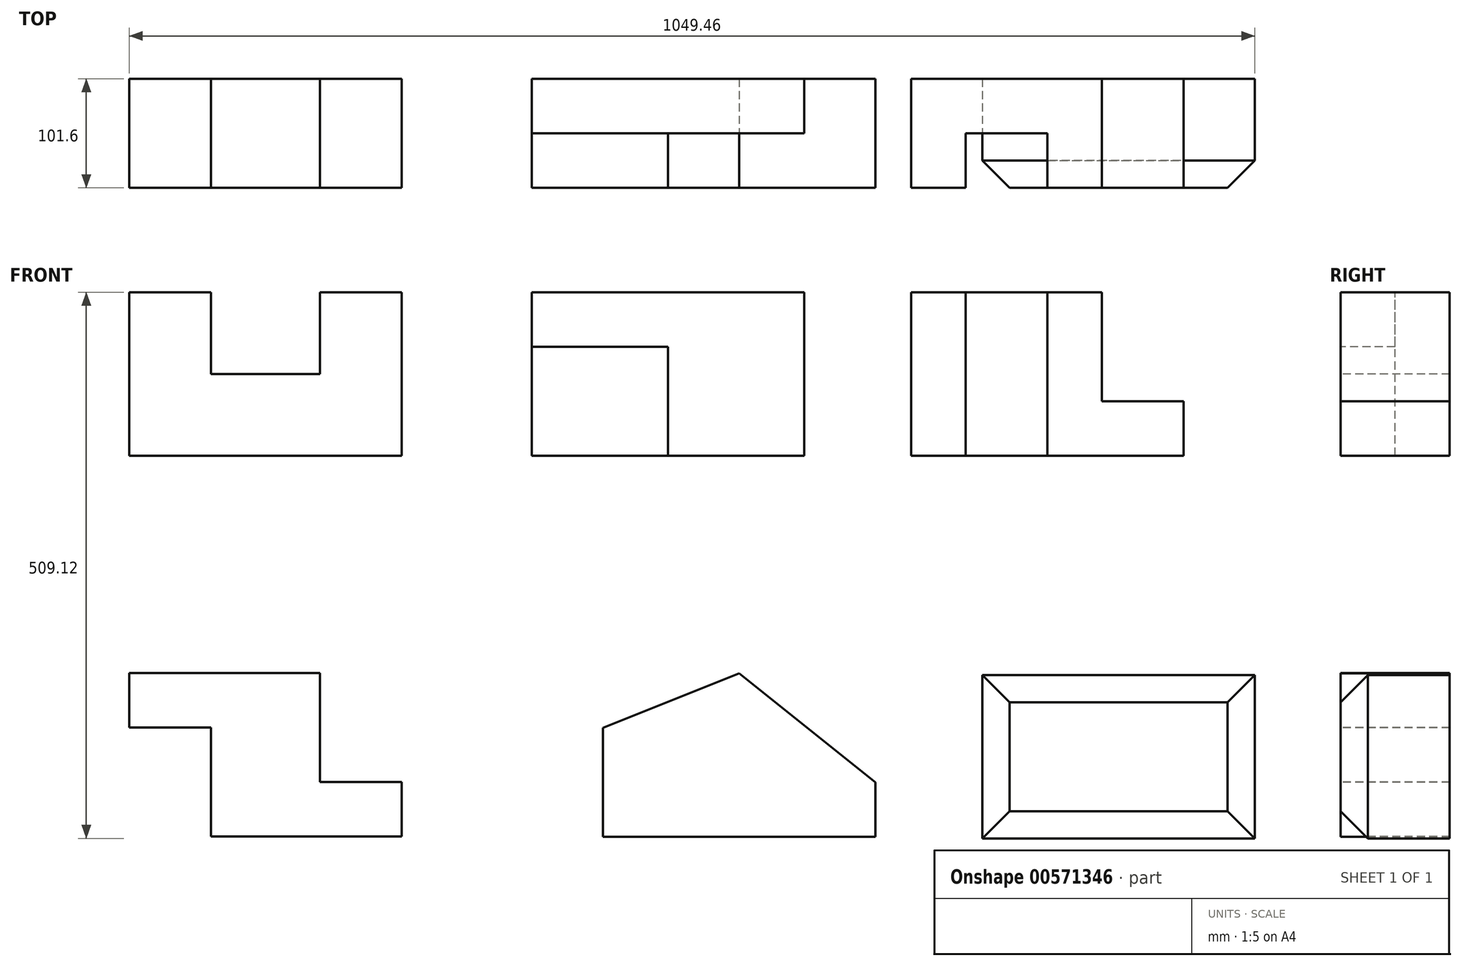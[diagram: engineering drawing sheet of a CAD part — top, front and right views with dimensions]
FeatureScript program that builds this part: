
annotation { "Feature Type Name" : "Feature", "Feature Type Description" : "" }
export const myFeature = defineFeature(function(context is Context, id is Id, definition is map)
    precondition{}
    {
        {
            var Q0;
            Q0=qCreatedBy(makeId("Front.planeOp"),FACE);
            var sketch = newSketch(context, id + "F0", { "sketchPlane" : qUnion([Q0])});
            skLineSegment(sketch, "E0", {"start": v(0, 0) * mm, "end": v(254, 0) * mm});
            skLineSegment(sketch, "E1", {"start": v(254, 0) * mm, "end": v(254, 152.4) * mm});
            skLineSegment(sketch, "E2", {"start": v(254, 152.4) * mm, "end": v(177.8, 152.4) * mm});
            skLineSegment(sketch, "E3", {"start": v(177.8, 152.4) * mm, "end": v(177.8, 76.2) * mm});
            skLineSegment(sketch, "E4", {"start": v(177.8, 76.2) * mm, "end": v(76.2, 76.2) * mm});
            skLineSegment(sketch, "E5", {"start": v(76.2, 76.2) * mm, "end": v(76.2, 152.4) * mm});
            skLineSegment(sketch, "E6", {"start": v(76.2, 152.4) * mm, "end": v(0, 152.4) * mm});
            skLineSegment(sketch, "E7", {"start": v(0, 152.4) * mm, "end": v(0, 0) * mm});
            skSolve(sketch);
        }
        {
            var Q0;
            Q0=makeQuery(id+"F0.imprint","IMPRINT",FACE,{"disambiguationData":[TD([[makeQuery(id+"F0.imprint","IMPRINT",EDGE,{"derivedFrom":sQuery(id+"F0.wireOp",EDGE,"E0")}),1.0]])]});
            extrude(context, id + "F1", {"entities" : qUnion([Q0]), "oppositeDirection" : true, "depth" : 101.6 * mm, "offsetDistance" : 25.4 * mm});
        }
        {
            var Q0;
            Q0=qCreatedBy(makeId("Front.planeOp"),FACE);
            var sketch = newSketch(context, id + "F2", { "sketchPlane" : qUnion([Q0])});
            skLineSegment(sketch, "E8.bottom", {"start": v(375.22, 0) * mm, "end": v(629.22, 0) * mm});
            skLineSegment(sketch, "E8.top", {"start": v(375.22, 152.4) * mm, "end": v(629.22, 152.4) * mm});
            skLineSegment(sketch, "E8.left", {"start": v(375.22, 0) * mm, "end": v(375.22, 152.4) * mm});
            skLineSegment(sketch, "E8.right", {"start": v(629.22, 0) * mm, "end": v(629.22, 152.4) * mm});
            skSolve(sketch);
        }
        {
            var Q0;
            Q0=makeQuery(id+"F2.imprint","IMPRINT",FACE,{"disambiguationData":[TD([[makeQuery(id+"F2.imprint","IMPRINT",EDGE,{"derivedFrom":sQuery(id+"F2.wireOp",EDGE,"E8.bottom")}),1.0]])]});
            extrude(context, id + "F3", {"entities" : qUnion([Q0]), "oppositeDirection" : true, "depth" : 101.6 * mm, "offsetDistance" : 25.4 * mm});
        }
        {
            var Q0;
            Q0=makeQuery(id+"F3.opExtrude","SWEPT_FACE",FACE,{"disambiguationData":[OSD([sQuery(id+"F2.wireOp",EDGE,"E8.top")])]});
            var sketch = newSketch(context, id + "F4", { "sketchPlane" : qUnion([Q0])});
            skLineSegment(sketch, "E9.bottom", {"start": v(629.22, 0) * mm, "end": v(502.22, 0) * mm});
            skLineSegment(sketch, "E9.top", {"start": v(629.22, 50.8) * mm, "end": v(502.22, 50.8) * mm});
            skLineSegment(sketch, "E9.left", {"start": v(629.22, 0) * mm, "end": v(629.22, 50.8) * mm});
            skLineSegment(sketch, "E9.right", {"start": v(502.22, 0) * mm, "end": v(502.22, 50.8) * mm});
            skSolve(sketch);
        }
        {
            var Q0;
            Q0=makeQuery(id+"F4.imprint","IMPRINT",FACE,{"disambiguationData":[TD([[makeQuery(id+"F4.imprint","IMPRINT",EDGE,{"derivedFrom":sQuery(id+"F4.wireOp",EDGE,"E9.bottom")}),1.0]])]});
            extrude(context, id + "F5", {"entities" : qUnion([Q0]), "operationType" : NewBodyOperationType.REMOVE, "oppositeDirection" : true, "depth" : 152.4 * mm, "offsetDistance" : 25.4 * mm});
        }
        {
            var Q0;
            Q0=makeQuery(id+"F3.opExtrude","CAP_FACE",FACE,{"disambiguationData":[OSD([sQuery(id+"F2.wireOp",EDGE,"E8.bottom"),sQuery(id+"F2.wireOp",EDGE,"E8.top"),sQuery(id+"F2.wireOp",EDGE,"E8.left"),sQuery(id+"F2.wireOp",EDGE,"E8.right")])],"isStart":true});
            var sketch = newSketch(context, id + "F6", { "sketchPlane" : qUnion([Q0])});
            skLineSegment(sketch, "E10", {"start": v(502.22, 152.4) * mm, "end": v(375.22, 152.4) * mm});
            skLineSegment(sketch, "E11", {"start": v(375.22, 152.4) * mm, "end": v(375.22, 101.6) * mm});
            skLineSegment(sketch, "E12", {"start": v(375.22, 101.6) * mm, "end": v(502.22, 101.6) * mm});
            skSolve(sketch);
        }
        {
            var Q0;
            Q0 = qSketchRegion(id + "F6", true);
            var Q1;
            {var subQ0=sQuery(id+"F6.wireOp",EDGE,"E10");Q1=makeQuery(id+"F6.imprint","IMPRINT",FACE,{"disambiguationData":[TD([[makeQuery(id+"F6.imprint","IMPRINT",EDGE,{"derivedFrom":subQ0}),-1.0]])]});}
            extrude(context, id + "F7", {"entities" : qUnion([Q0, Q1]), "operationType" : NewBodyOperationType.REMOVE, "oppositeDirection" : true, "depth" : 50.8 * mm, "offsetDistance" : 25.4 * mm});
        }
        {
            var Q0;
            Q0=qCreatedBy(makeId("Front.planeOp"),FACE);
            var sketch = newSketch(context, id + "F8", { "sketchPlane" : qUnion([Q0])});
            skLineSegment(sketch, "E13.bottom", {"start": v(729.02, 0) * mm, "end": v(983.02, 0) * mm});
            skLineSegment(sketch, "E13.top", {"start": v(729.02, 152.4) * mm, "end": v(983.02, 152.4) * mm});
            skLineSegment(sketch, "E13.left", {"start": v(729.02, 0) * mm, "end": v(729.02, 152.4) * mm});
            skLineSegment(sketch, "E13.right", {"start": v(983.02, 0) * mm, "end": v(983.02, 152.4) * mm});
            skSolve(sketch);
        }
        {
            var Q0;
            Q0=makeQuery(id+"F8.imprint","IMPRINT",FACE,{"disambiguationData":[TD([[makeQuery(id+"F8.imprint","IMPRINT",EDGE,{"derivedFrom":sQuery(id+"F8.wireOp",EDGE,"E13.bottom")}),1.0]])]});
            extrude(context, id + "F9", {"entities" : qUnion([Q0]), "oppositeDirection" : true, "depth" : 101.6 * mm, "offsetDistance" : 25.4 * mm});
        }
        {
            var Q0;
            Q0=makeQuery(id+"F9.opExtrude","CAP_FACE",FACE,{"disambiguationData":[OSD([sQuery(id+"F8.wireOp",EDGE,"E13.bottom"),sQuery(id+"F8.wireOp",EDGE,"E13.top"),sQuery(id+"F8.wireOp",EDGE,"E13.left"),sQuery(id+"F8.wireOp",EDGE,"E13.right")])],"isStart":true});
            var sketch = newSketch(context, id + "F10", { "sketchPlane" : qUnion([Q0])});
            skLineSegment(sketch, "E14", {"start": v(983.02, 152.4) * mm, "end": v(906.82, 152.4) * mm});
            skLineSegment(sketch, "E15", {"start": v(906.82, 152.4) * mm, "end": v(906.82, 50.8) * mm});
            skLineSegment(sketch, "E16", {"start": v(906.82, 50.8) * mm, "end": v(983.02, 50.8) * mm});
            skSolve(sketch);
        }
        {
            var Q0;
            {var subQ0=sQuery(id+"F10.wireOp",EDGE,"E14");Q0=makeQuery(id+"F10.imprint","IMPRINT",FACE,{"disambiguationData":[TD([[makeQuery(id+"F10.imprint","IMPRINT",EDGE,{"derivedFrom":subQ0}),-1.0]])]});}
            extrude(context, id + "F11", {"entities" : qUnion([Q0]), "operationType" : NewBodyOperationType.REMOVE, "oppositeDirection" : true, "depth" : 101.6 * mm, "offsetDistance" : 25.4 * mm});
        }
        {
            var Q0;
            Q0=makeQuery(id+"F9.opExtrude","SWEPT_FACE",FACE,{"disambiguationData":[OSD([sQuery(id+"F8.wireOp",EDGE,"E13.top")])]});
            var sketch = newSketch(context, id + "F12", { "sketchPlane" : qUnion([Q0])});
            skLineSegment(sketch, "E17", {"start": v(779.82, 0) * mm, "end": v(779.82, 50.8) * mm});
            skLineSegment(sketch, "E18", {"start": v(779.82, 50.8) * mm, "end": v(856.02, 50.8) * mm});
            skLineSegment(sketch, "E19", {"start": v(856.02, 50.8) * mm, "end": v(856.02, 0) * mm});
            skSolve(sketch);
        }
        {
            var Q0;
            {var subQ0=sQuery(id+"F12.wireOp",EDGE,"E17");Q0=makeQuery(id+"F12.imprint","IMPRINT",FACE,{"disambiguationData":[TD([[makeQuery(id+"F12.imprint","IMPRINT",EDGE,{"derivedFrom":subQ0}),-1.0]])]});}
            extrude(context, id + "F13", {"entities" : qUnion([Q0]), "operationType" : NewBodyOperationType.REMOVE, "oppositeDirection" : true, "depth" : 152.4 * mm, "offsetDistance" : 25.4 * mm});
        }
        {
            var Q0;
            Q0=qCreatedBy(makeId("Front.planeOp"),FACE);
            var sketch = newSketch(context, id + "F14", { "sketchPlane" : qUnion([Q0])});
            skLineSegment(sketch, "E20.bottom", {"start": v(0, -202.4) * mm, "end": v(254, -202.4) * mm});
            skLineSegment(sketch, "E20.top", {"start": v(0, -354.8) * mm, "end": v(254, -354.8) * mm});
            skLineSegment(sketch, "E20.left", {"start": v(0, -202.4) * mm, "end": v(0, -354.8) * mm});
            skLineSegment(sketch, "E20.right", {"start": v(254, -202.4) * mm, "end": v(254, -354.8) * mm});
            skSolve(sketch);
        }
        {
            var Q0;
            Q0=makeQuery(id+"F14.imprint","IMPRINT",FACE,{"disambiguationData":[TD([[makeQuery(id+"F14.imprint","IMPRINT",EDGE,{"derivedFrom":sQuery(id+"F14.wireOp",EDGE,"E20.bottom")}),-1.0]])]});
            extrude(context, id + "F15", {"entities" : qUnion([Q0]), "oppositeDirection" : true, "depth" : 101.6 * mm, "offsetDistance" : 25.4 * mm});
        }
        {
            var Q0;
            Q0=makeQuery(id+"F15.opExtrude","CAP_FACE",FACE,{"disambiguationData":[OSD([sQuery(id+"F14.wireOp",EDGE,"E20.bottom"),sQuery(id+"F14.wireOp",EDGE,"E20.top"),sQuery(id+"F14.wireOp",EDGE,"E20.left"),sQuery(id+"F14.wireOp",EDGE,"E20.right")])],"isStart":true});
            var sketch = newSketch(context, id + "F16", { "sketchPlane" : qUnion([Q0])});
            skLineSegment(sketch, "E21", {"start": v(0, -354.8) * mm, "end": v(76.2, -354.8) * mm});
            skLineSegment(sketch, "E22", {"start": v(76.2, -354.8) * mm, "end": v(76.2, -253.2) * mm});
            skLineSegment(sketch, "E23", {"start": v(76.2, -253.2) * mm, "end": v(0, -253.2) * mm});
            skSolve(sketch);
        }
        {
            var Q0;
            {var subQ0=sQuery(id+"F16.wireOp",EDGE,"E21");Q0=makeQuery(id+"F16.imprint","IMPRINT",FACE,{"disambiguationData":[TD([[makeQuery(id+"F16.imprint","IMPRINT",EDGE,{"derivedFrom":subQ0}),1.0]])]});}
            extrude(context, id + "F17", {"entities" : qUnion([Q0]), "operationType" : NewBodyOperationType.REMOVE, "oppositeDirection" : true, "depth" : 101.6 * mm, "offsetDistance" : 25.4 * mm});
        }
        {
            var Q0;
            Q0=makeQuery(id+"F15.opExtrude","CAP_FACE",FACE,{"disambiguationData":[OSD([sQuery(id+"F14.wireOp",EDGE,"E20.bottom"),sQuery(id+"F14.wireOp",EDGE,"E20.top"),sQuery(id+"F14.wireOp",EDGE,"E20.left"),sQuery(id+"F14.wireOp",EDGE,"E20.right")])],"isStart":true});
            var sketch = newSketch(context, id + "F18", { "sketchPlane" : qUnion([Q0])});
            skLineSegment(sketch, "E24.bottom", {"start": v(254, -202.4) * mm, "end": v(177.8, -202.4) * mm});
            skLineSegment(sketch, "E24.top", {"start": v(254, -304) * mm, "end": v(177.8, -304) * mm});
            skLineSegment(sketch, "E24.left", {"start": v(254, -202.4) * mm, "end": v(254, -304) * mm});
            skLineSegment(sketch, "E24.right", {"start": v(177.8, -202.4) * mm, "end": v(177.8, -304) * mm});
            skSolve(sketch);
        }
        {
            var Q0;
            Q0=makeQuery(id+"F18.imprint","IMPRINT",FACE,{"disambiguationData":[TD([[makeQuery(id+"F18.imprint","IMPRINT",EDGE,{"derivedFrom":sQuery(id+"F18.wireOp",EDGE,"E24.bottom")}),-1.0]])]});
            extrude(context, id + "F19", {"entities" : qUnion([Q0]), "operationType" : NewBodyOperationType.REMOVE, "oppositeDirection" : true, "depth" : 101.6 * mm, "offsetDistance" : 25.4 * mm});
        }
        {
            var Q0;
            Q0=qCreatedBy(makeId("Front.planeOp"),FACE);
            var sketch = newSketch(context, id + "F20", { "sketchPlane" : qUnion([Q0])});
            skLineSegment(sketch, "E25.bottom", {"start": v(441.77, -355.41) * mm, "end": v(695.77, -355.41) * mm});
            skLineSegment(sketch, "E25.top", {"start": v(441.77, -203.01) * mm, "end": v(695.77, -203.01) * mm});
            skLineSegment(sketch, "E25.left", {"start": v(441.77, -355.41) * mm, "end": v(441.77, -203.01) * mm});
            skLineSegment(sketch, "E25.right", {"start": v(695.77, -355.41) * mm, "end": v(695.77, -203.01) * mm});
            skSolve(sketch);
        }
        {
            var Q0;
            Q0=makeQuery(id+"F20.imprint","IMPRINT",FACE,{"disambiguationData":[TD([[makeQuery(id+"F20.imprint","IMPRINT",EDGE,{"derivedFrom":sQuery(id+"F20.wireOp",EDGE,"E25.bottom")}),1.0]])]});
            extrude(context, id + "F21", {"entities" : qUnion([Q0]), "oppositeDirection" : true, "depth" : 101.6 * mm, "offsetDistance" : 25.4 * mm});
        }
        {
            var Q0;
            Q0=makeQuery(id+"F21.opExtrude","CAP_FACE",FACE,{"disambiguationData":[OSD([sQuery(id+"F20.wireOp",EDGE,"E25.bottom"),sQuery(id+"F20.wireOp",EDGE,"E25.top"),sQuery(id+"F20.wireOp",EDGE,"E25.left"),sQuery(id+"F20.wireOp",EDGE,"E25.right")])],"isStart":true});
            var sketch = newSketch(context, id + "F22", { "sketchPlane" : qUnion([Q0])});
            skLineSegment(sketch, "E26", {"start": v(441.77, -253.81) * mm, "end": v(441.77, -203.01) * mm});
            skLineSegment(sketch, "E27", {"start": v(441.77, -203.01) * mm, "end": v(568.77, -203.01) * mm});
            skLineSegment(sketch, "E28", {"start": v(441.77, -253.81) * mm, "end": v(568.77, -203.01) * mm});
            skSolve(sketch);
        }
        {
            var Q0;
            Q0=makeQuery(id+"F22.imprint","IMPRINT",FACE,{"disambiguationData":[TD([[makeQuery(id+"F22.imprint","IMPRINT",EDGE,{"derivedFrom":sQuery(id+"F22.wireOp",EDGE,"E26")}),-1.0]])]});
            extrude(context, id + "F23", {"entities" : qUnion([Q0]), "operationType" : NewBodyOperationType.REMOVE, "oppositeDirection" : true, "depth" : 101.6 * mm, "offsetDistance" : 25.4 * mm});
        }
        {
            var Q0;
            Q0=makeQuery(id+"F21.opExtrude","CAP_FACE",FACE,{"disambiguationData":[OSD([sQuery(id+"F20.wireOp",EDGE,"E25.bottom"),sQuery(id+"F20.wireOp",EDGE,"E25.top"),sQuery(id+"F20.wireOp",EDGE,"E25.left"),sQuery(id+"F20.wireOp",EDGE,"E25.right")])],"isStart":true});
            var sketch = newSketch(context, id + "F24", { "sketchPlane" : qUnion([Q0])});
            skLineSegment(sketch, "E29", {"start": v(695.77, -304.61) * mm, "end": v(568.77, -203.01) * mm});
            skLineSegment(sketch, "E30", {"start": v(568.77, -203.01) * mm, "end": v(695.77, -203.01) * mm});
            skLineSegment(sketch, "E31", {"start": v(695.77, -203.01) * mm, "end": v(695.77, -304.61) * mm});
            skSolve(sketch);
        }
        {
            var Q0;
            Q0=makeQuery(id+"F24.imprint","IMPRINT",FACE,{"disambiguationData":[TD([[makeQuery(id+"F24.imprint","IMPRINT",EDGE,{"derivedFrom":sQuery(id+"F24.wireOp",EDGE,"E29")}),-1.0]])]});
            extrude(context, id + "F25", {"entities" : qUnion([Q0]), "operationType" : NewBodyOperationType.REMOVE, "oppositeDirection" : true, "depth" : 101.6 * mm, "offsetDistance" : 25.4 * mm});
        }
        {
            var Q0;
            Q0=qCreatedBy(makeId("Front.planeOp"),FACE);
            var sketch = newSketch(context, id + "F26", { "sketchPlane" : qUnion([Q0])});
            skLineSegment(sketch, "E32.bottom", {"start": v(795.46, -356.72) * mm, "end": v(1049.46, -356.72) * mm});
            skLineSegment(sketch, "E32.top", {"start": v(795.46, -204.32) * mm, "end": v(1049.46, -204.32) * mm});
            skLineSegment(sketch, "E32.left", {"start": v(795.46, -356.72) * mm, "end": v(795.46, -204.32) * mm});
            skLineSegment(sketch, "E32.right", {"start": v(1049.46, -356.72) * mm, "end": v(1049.46, -204.32) * mm});
            skSolve(sketch);
        }
        {
            var Q0;
            Q0=makeQuery(id+"F26.imprint","IMPRINT",FACE,{"disambiguationData":[TD([[makeQuery(id+"F26.imprint","IMPRINT",EDGE,{"derivedFrom":sQuery(id+"F26.wireOp",EDGE,"E32.bottom")}),1.0]])]});
            extrude(context, id + "F27", {"entities" : qUnion([Q0]), "oppositeDirection" : true, "depth" : 101.6 * mm, "offsetDistance" : 25.4 * mm});
        }
        {
            var Q0;
            Q0=makeQuery(id+"F27.opExtrude","CAP_EDGE",EDGE,{"disambiguationData":[OSD([sQuery(id+"F26.wireOp",EDGE,"E32.top")])],"isStart":true});
            var Q1;
            Q1=makeQuery(id+"F27.opExtrude","CAP_EDGE",EDGE,{"disambiguationData":[OSD([sQuery(id+"F26.wireOp",EDGE,"E32.right")])],"isStart":true});
            var Q2;
            Q2=makeQuery(id+"F27.opExtrude","CAP_EDGE",EDGE,{"disambiguationData":[OSD([sQuery(id+"F26.wireOp",EDGE,"E32.bottom")])],"isStart":true});
            var Q3;
            Q3=makeQuery(id+"F27.opExtrude","CAP_EDGE",EDGE,{"disambiguationData":[OSD([sQuery(id+"F26.wireOp",EDGE,"E32.left")])],"isStart":true});
            chamfer(context, id + "F28", {"entities" : qUnion([Q0, Q1, Q2, Q3]), "width" : 25.4 * mm, "tangentPropagation" : true});
        }
    });
